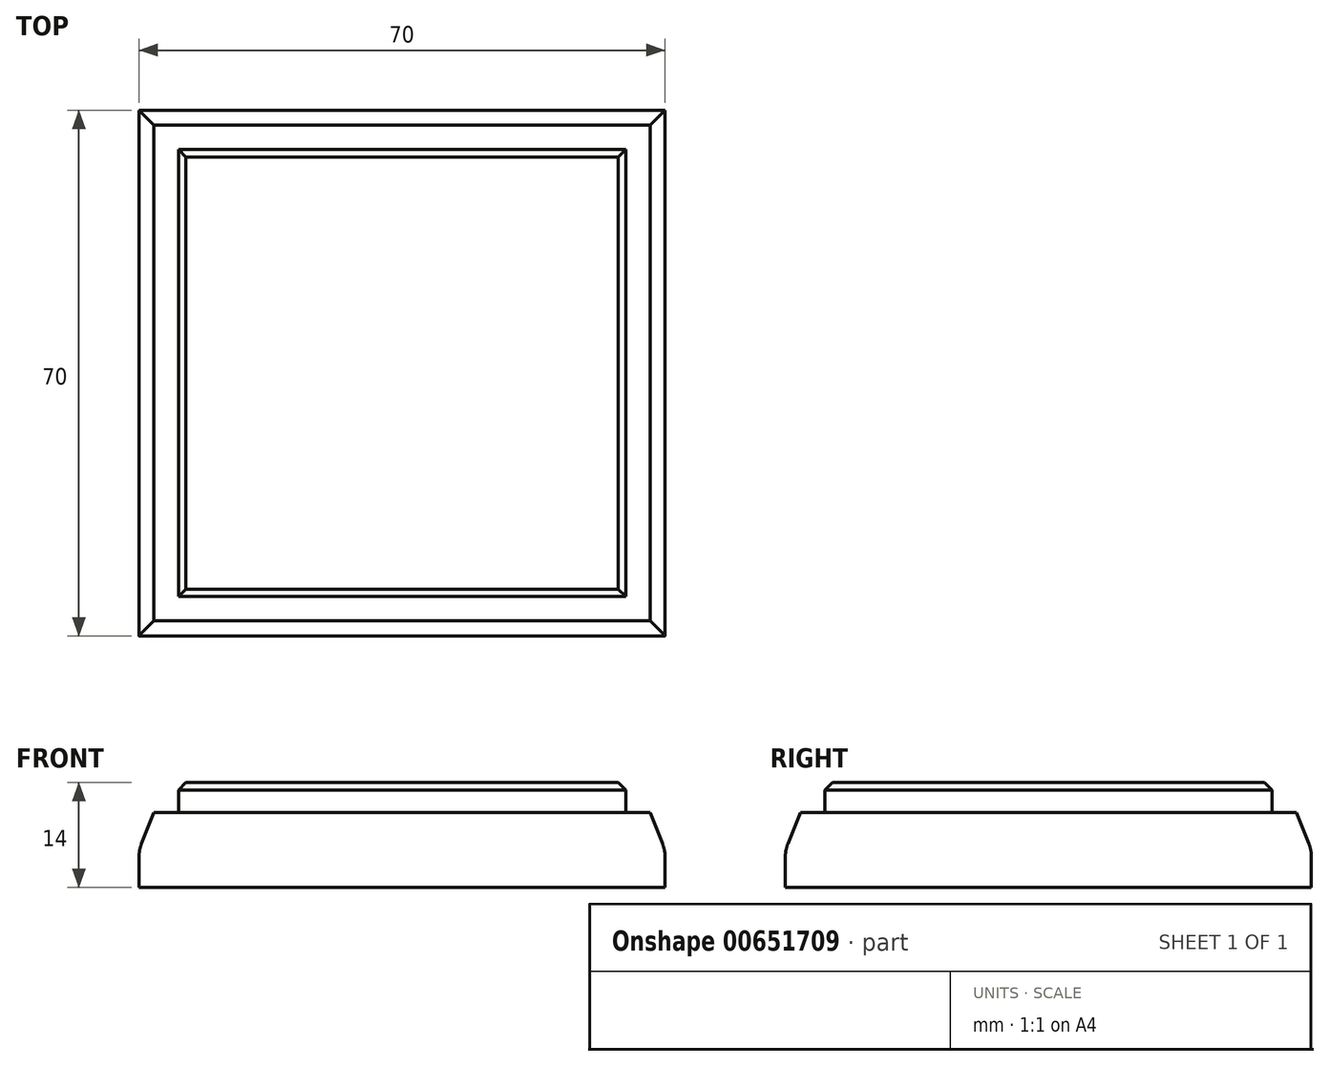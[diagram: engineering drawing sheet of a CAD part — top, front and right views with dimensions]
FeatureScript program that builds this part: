
annotation { "Feature Type Name" : "Feature", "Feature Type Description" : "" }
export const myFeature = defineFeature(function(context is Context, id is Id, definition is map)
    precondition{}
    {
        {
            var Q0;
            Q0=qCreatedBy(makeId("Top.planeOp"),FACE);
            var sketch = newSketch(context, id + "F0", { "sketchPlane" : qUnion([Q0])});
            skLineSegment(sketch, "E0.bottom", {"start": v(35, -35) * mm, "end": v(-35, -35) * mm});
            skLineSegment(sketch, "E0.top", {"start": v(35, 35) * mm, "end": v(-35, 35) * mm});
            skLineSegment(sketch, "E0.left", {"start": v(35, -35) * mm, "end": v(35, 35) * mm});
            skLineSegment(sketch, "E0.right", {"start": v(-35, -35) * mm, "end": v(-35, 35) * mm});
            skPoint(sketch, "E0.middle", {"position": v(0, 0) * mm});
            skLineSegment(sketch, "E1.bottom", {"start": v(29.75, -29.75) * mm, "end": v(-29.75, -29.75) * mm});
            skLineSegment(sketch, "E1.top", {"start": v(29.75, 29.75) * mm, "end": v(-29.75, 29.75) * mm});
            skLineSegment(sketch, "E1.left", {"start": v(29.75, -29.75) * mm, "end": v(29.75, 29.75) * mm});
            skLineSegment(sketch, "E1.right", {"start": v(-29.75, -29.75) * mm, "end": v(-29.75, 29.75) * mm});
            skSolve(sketch);
        }
        {
            var Q0;
            Q0=makeQuery(id+"F0.imprint","IMPRINT",FACE,{"disambiguationData":[TD([[makeQuery(id+"F0.imprint","IMPRINT",EDGE,{"derivedFrom":sQuery(id+"F0.wireOp",EDGE,"E1.bottom")}),-1.0]])]});
            extrude(context, id + "F1", {"entities" : qUnion([Q0]), "depth" : 14 * mm, "offsetDistance" : 25 * mm});
        }
        {
            var Q0;
            Q0=makeQuery(id+"F0.imprint","IMPRINT",FACE,{"disambiguationData":[TD([[makeQuery(id+"F0.imprint","IMPRINT",EDGE,{"derivedFrom":sQuery(id+"F0.wireOp",EDGE,"E0.bottom")}),-1.0]])]});
            extrude(context, id + "F2", {"entities" : qUnion([Q0]), "operationType" : NewBodyOperationType.ADD, "depth" : 10 * mm, "offsetDistance" : 25 * mm});
        }
        {
            var Q0;
            Q0=makeQuery(id+"F1.opExtrude","CAP_FACE",FACE,{"disambiguationData":[OSD([sQuery(id+"F0.wireOp",EDGE,"E1.bottom"),sQuery(id+"F0.wireOp",EDGE,"E1.top"),sQuery(id+"F0.wireOp",EDGE,"E1.left"),sQuery(id+"F0.wireOp",EDGE,"E1.right")])],"isStart":false});
            chamfer(context, id + "F3", {"entities" : qUnion([Q0]), "width" : 1 * mm, "tangentPropagation" : true});
        }
        {
            var Q0;
            Q0=makeQuery(id+"F2.opExtrude","CAP_EDGE",EDGE,{"disambiguationData":[OSD([sQuery(id+"F0.wireOp",EDGE,"E0.bottom")])],"isStart":false});
            var Q1;
            Q1=makeQuery(id+"F2.opExtrude","CAP_EDGE",EDGE,{"disambiguationData":[OSD([sQuery(id+"F0.wireOp",EDGE,"E0.left")])],"isStart":false});
            var Q2;
            Q2=makeQuery(id+"F2.opExtrude","CAP_EDGE",EDGE,{"disambiguationData":[OSD([sQuery(id+"F0.wireOp",EDGE,"E0.top")])],"isStart":false});
            var Q3;
            Q3=makeQuery(id+"F2.opExtrude","CAP_EDGE",EDGE,{"disambiguationData":[OSD([sQuery(id+"F0.wireOp",EDGE,"E0.right")])],"isStart":false});
            chamfer(context, id + "F4", {"entities" : qUnion([Q0, Q1, Q2, Q3]), "chamferType" : ChamferType.TWO_OFFSETS, "width1" : 5 * mm, "oppositeDirection" : false, "width2" : 2 * mm, "tangentPropagation" : true});
        }
        {
            var Q0;
            {var subQ0=sQuery(id+"F0.wireOp",EDGE,"E0.left");Q0=makeQuery(id+"F4.opChamfer","BLEND_EDGE",EDGE,{"blendedFrom":[makeQuery(id+"F2.opExtrude","CAP_EDGE",EDGE,{"disambiguationData":[OSD([subQ0])],"isStart":false}),makeQuery(id+"F2.opExtrude","SWEPT_FACE",FACE,{"disambiguationData":[OSD([subQ0])]})],"blendedInto":[makeQuery(id+"F2.opExtrude","SWEPT_FACE",FACE,{"disambiguationData":[OSD([subQ0])]})]});}
            var Q1;
            {var subQ0=sQuery(id+"F0.wireOp",EDGE,"E0.bottom");Q1=makeQuery(id+"F4.opChamfer","BLEND_EDGE",EDGE,{"blendedFrom":[makeQuery(id+"F2.opExtrude","CAP_EDGE",EDGE,{"disambiguationData":[OSD([subQ0])],"isStart":false}),makeQuery(id+"F2.opExtrude","SWEPT_FACE",FACE,{"disambiguationData":[OSD([subQ0])]})],"blendedInto":[makeQuery(id+"F2.opExtrude","SWEPT_FACE",FACE,{"disambiguationData":[OSD([subQ0])]})]});}
            var Q2;
            {var subQ0=sQuery(id+"F0.wireOp",EDGE,"E0.right");Q2=makeQuery(id+"F4.opChamfer","BLEND_EDGE",EDGE,{"blendedFrom":[makeQuery(id+"F2.opExtrude","CAP_EDGE",EDGE,{"disambiguationData":[OSD([subQ0])],"isStart":false}),makeQuery(id+"F2.opExtrude","SWEPT_FACE",FACE,{"disambiguationData":[OSD([subQ0])]})],"blendedInto":[makeQuery(id+"F2.opExtrude","SWEPT_FACE",FACE,{"disambiguationData":[OSD([subQ0])]})]});}
            var Q3;
            {var subQ0=sQuery(id+"F0.wireOp",EDGE,"E0.top");Q3=makeQuery(id+"F4.opChamfer","BLEND_EDGE",EDGE,{"blendedFrom":[makeQuery(id+"F2.opExtrude","CAP_EDGE",EDGE,{"disambiguationData":[OSD([subQ0])],"isStart":false}),makeQuery(id+"F2.opExtrude","SWEPT_FACE",FACE,{"disambiguationData":[OSD([subQ0])]})],"blendedInto":[makeQuery(id+"F2.opExtrude","SWEPT_FACE",FACE,{"disambiguationData":[OSD([subQ0])]})]});}
            fillet(context, id + "F5", {"entities" : qUnion([Q0, Q1, Q2, Q3]), "radius" : 5 * mm, "tangentPropagation" : true, "allowEdgeOverflow" : false});
        }
    });
